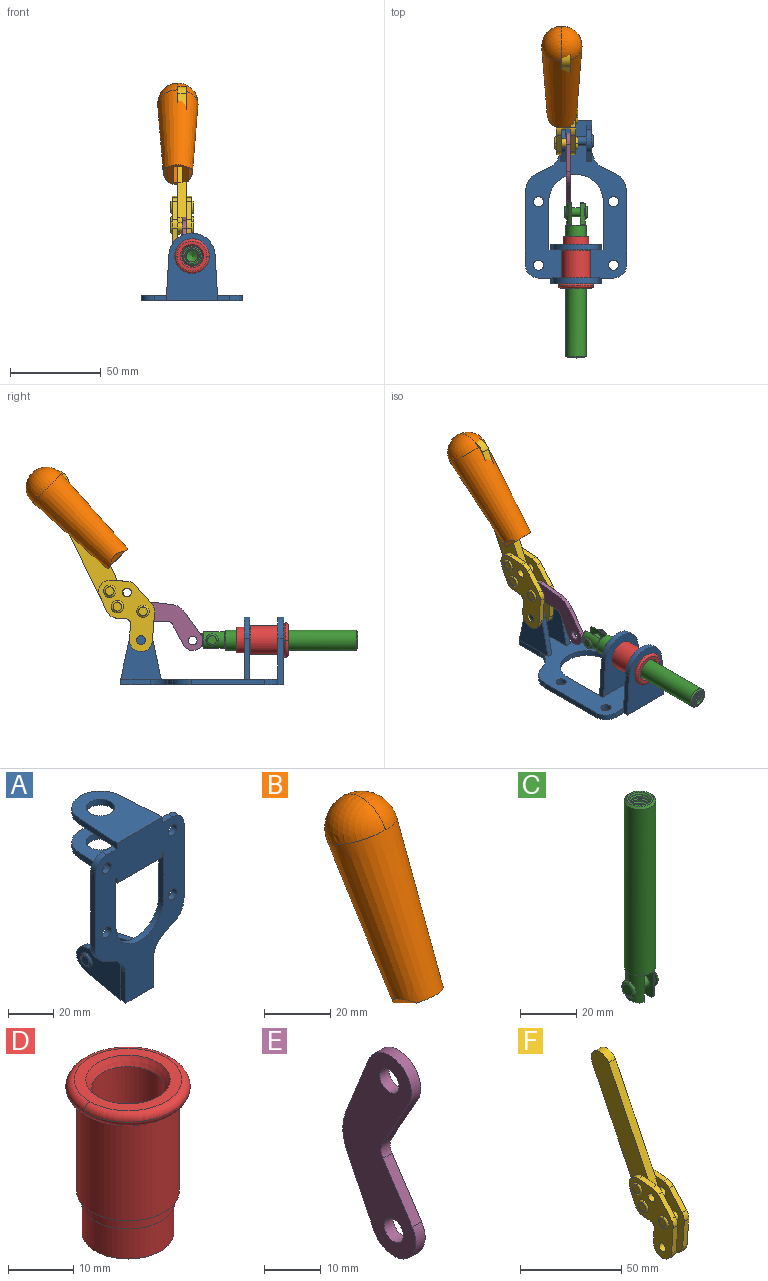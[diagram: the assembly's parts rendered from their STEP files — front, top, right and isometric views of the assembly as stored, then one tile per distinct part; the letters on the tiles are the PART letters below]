
ASSEMBLY  parts=6 mates=5
PART A: 55 faces, bbox 55.7x37.4x89.8 mm
  f0: torus R=2.41mm, axis (-1,0,0), area 15mm2, adj f11,f15,f25
  f1: torus R=2.41mm, axis (-1,0,0), area 15mm2, adj f10,f12,f22
  f2: cylinder r=2.78mm len=5.56mm, axis (0,-1,0), area 54.2mm2, adj f30,f54
  f3: cylinder r=14.99mm len=29.97mm, axis (0,-1,0), area 145.9mm2, adj f30,f49,f53,f54
  f4: cylinder r=2.78mm len=5.56mm, axis (0,-1,0), area 54.2mm2, adj f30,f54
  f5: cylinder r=2.78mm len=5.56mm, axis (0,-1,0), area 54.2mm2, adj f30,f54
  f6: cylinder r=2.78mm len=5.56mm, axis (0,-1,0), area 54.2mm2, adj f30,f54
  f7: cylinder r=6.35mm len=12.7mm, axis (0,0,1), area 123.6mm2, adj f27,f51
  f8: cylinder r=6.35mm len=12.7mm, axis (0,0,-1), area 124.7mm2, adj f21,f35
  f9: cylinder r=2.41mm len=11.18mm, axis (-1,0,0), area 169.4mm2, adj f16,f19
  f10: plane 4.83x4.83mm, normal (1,0,0), area 18.3mm2, adj f1,f12
  f11: plane 4.83x4.83mm, normal (-1,0,0), area 18.3mm2, adj f0,f15
  f12: torus R=2.41mm, axis (-1,0,0), area 15mm2, adj f1,f10,f22
  f13: cylinder r=6.35mm len=12.41mm, axis (1,0,0), area 53.4mm2, adj f18,f19,f22,f23
  f14: cylinder r=6.35mm len=12.41mm, axis (-1,0,0), area 53.4mm2, adj f16,f17,f24,f25
  f15: torus R=2.41mm, axis (-1,0,0), area 15mm2, adj f0,f11,f25
  f16: plane 27.86x22.35mm, normal (1,0,0), area 425.4mm2, adj f9,f14,f17,f24,f30
  f17: plane 22.86x4.97mm, normal (0,0.21,0.98), area 72.5mm2, adj f14,f16,f25,f30
  f18: plane 22.86x4.97mm, normal (0,0.21,0.98), area 72.5mm2, adj f13,f19,f22,f30
  f19: plane 27.86x22.35mm, normal (-1,0,0), area 425.4mm2, adj f9,f13,f18,f23,f30
  f20: cylinder r=12.7mm len=25.35mm, axis (0,0,-1), area 119.8mm2, adj f21,f34,f35,f36
  f21: plane 34.21x28.07mm, normal (0,0,-1), area 702.4mm2, adj f8,f20,f30,f34,f36
  f22: plane 27.96x22.45mm, normal (1,0,0), area 407.2mm2, adj f1,f12,f13,f18,f23,f30,f42,f43
  f23: plane 22.86x4.97mm, normal (0,0.21,-0.98), area 72.5mm2, adj f13,f19,f22,f44
  f24: plane 22.86x4.97mm, normal (0,0.21,-0.98), area 72.5mm2, adj f14,f16,f25,f44
  f25: plane 27.86x22.35mm, normal (-1,0,0), area 407.1mm2, adj f0,f14,f15,f17,f24,f30,f45,f46
  f26: plane 3.1x0.95mm, normal (0,0,-1), area 2.7mm2, adj f30,f49,f50,f54
  f27: plane 34.21x28.07mm, normal (0,0,1), area 702.4mm2, adj f7,f28,f30,f50,f52
  f28: cylinder r=12.7mm len=25.35mm, axis (0,0,1), area 118.8mm2, adj f27,f50,f51,f52
  f29: plane 3.1x0.95mm, normal (0,0,-1), area 2.7mm2, adj f30,f52,f53,f54
  f30: plane 86.54x55.63mm, normal (0,1,0), area 2362.9mm2, adj f2,f3,f4,f5,f6,f16,f17,f18
  f31: plane 40.56x3.1mm, normal (-1,0,0), area 125.7mm2, adj f30,f32,f48,f54
  f32: cylinder r=7.11mm len=7.11mm, axis (0,-1,0), area 34.6mm2, adj f30,f31,f33,f54
  f33: plane 6.67x3.1mm, normal (0,0,1), area 20.4mm2, adj f30,f32,f34,f54
  f34: plane 25.39x3.13mm, normal (-1,0.06,0), area 79.5mm2, adj f20,f21,f33,f35,f54
  f35: plane 37.31x28.45mm, normal (0,0,1), area 789.9mm2, adj f8,f20,f34,f36,f54
  f36: plane 25.39x3.13mm, normal (1,0.06,0), area 79.5mm2, adj f20,f21,f35,f37,f54
  f37: plane 6.67x3.1mm, normal (0,0,1), area 20.4mm2, adj f30,f36,f38,f54
  f38: cylinder r=7.11mm len=7.11mm, axis (0,-1,0), area 34.6mm2, adj f30,f37,f39,f54
  f39: plane 40.56x3.1mm, normal (1,0,0), area 125.7mm2, adj f30,f38,f40,f54
  f40: cylinder r=11.18mm len=10.16mm, axis (0,-1,0), area 39.5mm2, adj f30,f39,f41,f54
  f41: plane 6.09x3.1mm, normal (0.42,0,-0.91), area 20.8mm2, adj f30,f40,f42,f54
  f42: cylinder r=11.18mm len=9.41mm, axis (0,-1,0), area 37.2mm2, adj f22,f30,f41,f43,f54
  f43: plane 16.5x3.1mm, normal (1,0,0), area 51.1mm2, adj f22,f42,f44,f54
  f44: plane 17.37x3.1mm, normal (0,0,-1), area 53.8mm2, adj f23,f24,f30,f43,f45,f54
  f45: plane 16.5x3.1mm, normal (-1,0,0), area 51.1mm2, adj f25,f44,f46,f54
  f46: cylinder r=11.18mm len=9.41mm, axis (0,-1,0), area 37.2mm2, adj f25,f30,f45,f47,f54
  f47: plane 6.09x3.1mm, normal (-0.42,0,-0.91), area 20.8mm2, adj f30,f46,f48,f54
  f48: cylinder r=11.18mm len=10.16mm, axis (0,-1,0), area 39.5mm2, adj f30,f31,f47,f54
  f49: plane 26.54x3.1mm, normal (-1,0,0), area 82.3mm2, adj f3,f26,f30,f54
  f50: plane 25.39x3.1mm, normal (1,0.06,0), area 78.8mm2, adj f26,f27,f28,f51,f54
  f51: plane 37.31x28.45mm, normal (0,0,-1), area 789.9mm2, adj f7,f28,f50,f52,f54
  f52: plane 25.39x3.1mm, normal (-1,0.06,0), area 78.8mm2, adj f27,f28,f29,f51,f54
  f53: plane 26.54x3.1mm, normal (1,0,0), area 82.3mm2, adj f3,f29,f30,f54
  f54: plane 89.66x55.63mm, normal (0,-1,0), area 2678.5mm2, adj f2,f3,f4,f5,f6,f26,f29,f31
PART B: 11 faces, bbox 22.3x42.6x64.5 mm
  f0: sphere r=11.13mm, area 411.4mm2, adj f1,f8
  f1: cone r=11.11mm half-angle=3.3deg, axis (0,0.44,0.9), area 3251.8mm2, adj f0,f7,f8,f9,f10
  f2: cylinder r=6.16mm len=11.7mm, axis (1,0,0), area 89.5mm2, adj f3,f4,f5,f6
  f3: plane 60.23x36.75mm, normal (-1,0,0), area 763.6mm2, adj f2,f4,f6,f10
  f4: plane 51.37x25.05mm, normal (0,0.9,-0.44), area 264.2mm2, adj f2,f3,f5,f10
  f5: plane 60.23x36.75mm, normal (1,0,0), area 763.6mm2, adj f2,f4,f6,f10
  f6: plane 51.37x25.05mm, normal (0,-0.9,0.44), area 264.2mm2, adj f2,f3,f5,f10
  f7: plane 9.95x5.95mm, normal (0.71,-0.31,-0.64), area 25.8mm2, adj f1,f10
  f8: sphere r=11.13mm, area 411.4mm2, adj f0,f1
  f9: plane 9.95x5.95mm, normal (-0.71,-0.31,-0.64), area 25.8mm2, adj f1,f10
  f10: plane 14.27x11.38mm, normal (0,-0.44,-0.9), area 106.7mm2, adj f1,f3,f4,f5,f6,f7,f9
PART C: 48 faces, bbox 12.6x11.1x86.1 mm
  f0: torus R=2.41mm, axis (-1,0,0), area 15mm2, adj f30,f32,f34
  f1: torus R=2.41mm, axis (-1,0,0), area 15mm2, adj f29,f31,f33
  f2: cylinder r=5.54mm len=72.39mm, axis (0,0,1), area 2518.5mm2, adj f3,f4,f42,f43
  f3: cone r=5.54mm half-angle=45deg, axis (0,0,1), area 7.6mm2, adj f2,f5,f41
  f4: cone r=5.54mm half-angle=45deg, axis (0,0,-1), area 34.9mm2, adj f2,f39
  f5: cylinder r=5.08mm len=11.48mm, axis (0,0,1), area 108.3mm2, adj f3,f7,f8,f41
  f6: cylinder r=2.41mm len=4.83mm, axis (-1,0,0), area 71.2mm2, adj f40,f41
  f7: cylinder r=2.41mm len=4.83mm, axis (-1,0,0), area 7.6mm2, adj f5,f34
  f8: cone r=5.08mm half-angle=45deg, axis (0,0,1), area 10.6mm2, adj f5,f37,f41
  f9: cone r=3.98mm half-angle=45deg, axis (0,0,1), area 17.6mm2, adj f27,f39,f45,f46,f47
  f10: cylinder r=2.41mm len=4.83mm, axis (-1,0,0), area 7.6mm2, adj f33,f38
  f11: cylinder r=3.2mm len=6.4mm, axis (0,0,1), area 78.4mm2, adj f12,f28,f44,f45,f47
  f12: cylinder r=3.2mm len=6.4mm, axis (0,0,1), area 10.5mm2, adj f11,f13,f45,f47
  f13: cylinder r=3.2mm len=6.4mm, axis (0,0,1), area 10.5mm2, adj f12,f14,f45,f47
  f14: cylinder r=3.2mm len=6.4mm, axis (0,0,1), area 10.5mm2, adj f13,f15,f45,f47
  f15: cylinder r=3.2mm len=6.4mm, axis (0,0,1), area 10.5mm2, adj f14,f16,f45,f47
  f16: cylinder r=3.2mm len=6.4mm, axis (0,0,1), area 10.5mm2, adj f15,f17,f45,f47
  f17: cylinder r=3.2mm len=6.4mm, axis (0,0,1), area 10.5mm2, adj f16,f18,f45,f47
  f18: cylinder r=3.2mm len=6.4mm, axis (0,0,1), area 10.5mm2, adj f17,f19,f45,f47
  f19: cylinder r=3.2mm len=6.4mm, axis (0,0,1), area 10.5mm2, adj f18,f20,f45,f47
  f20: cylinder r=3.2mm len=6.4mm, axis (0,0,1), area 10.5mm2, adj f19,f21,f45,f47
  f21: cylinder r=3.2mm len=6.4mm, axis (0,0,1), area 10.5mm2, adj f20,f22,f45,f47
  f22: cylinder r=3.2mm len=6.4mm, axis (0,0,1), area 10.5mm2, adj f21,f23,f45,f47
  f23: cylinder r=3.2mm len=6.4mm, axis (0,0,1), area 10.5mm2, adj f22,f24,f45,f47
  f24: cylinder r=3.2mm len=6.4mm, axis (0,0,1), area 10.5mm2, adj f23,f25,f45,f47
  f25: cylinder r=3.2mm len=6.4mm, axis (0,0,1), area 10.5mm2, adj f24,f26,f45,f47
  f26: cylinder r=3.2mm len=6.4mm, axis (0,0,1), area 10.5mm2, adj f25,f27,f45,f47
  f27: cylinder r=3.2mm len=6.4mm, axis (0,0,1), area 7.4mm2, adj f9,f26,f45,f47
  f28: cone r=3.2mm half-angle=60deg, axis (0,0,1), area 37.2mm2, adj f11
  f29: plane 4.83x4.83mm, normal (-1,0,0), area 18.3mm2, adj f1,f31
  f30: plane 4.83x4.83mm, normal (1,0,0), area 18.3mm2, adj f0,f32
  f31: torus R=2.41mm, axis (-1,0,0), area 15mm2, adj f1,f29,f33
  f32: torus R=2.41mm, axis (-1,0,0), area 15mm2, adj f0,f30,f34
  f33: plane 6.83x6.83mm, normal (1,0,0), area 18.3mm2, adj f1,f10,f31
  f34: plane 6.83x6.83mm, normal (-1,0,0), area 18.3mm2, adj f0,f7,f32
  f35: cone r=5.08mm half-angle=45deg, axis (0,0,1), area 10.6mm2, adj f36,f38,f40
  f36: plane 7.25x1.97mm, normal (0,0,-1), area 10mm2, adj f35,f40
  f37: plane 7.25x1.97mm, normal (0,0,-1), area 10mm2, adj f8,f41
  f38: cylinder r=5.08mm len=11.48mm, axis (0,0,1), area 108.3mm2, adj f10,f35,f40,f42
  f39: plane 9.55x9.55mm, normal (0,0,1), area 22mm2, adj f4,f9
  f40: plane 12.76x10.09mm, normal (1,0,0), area 95.7mm2, adj f6,f35,f36,f38,f42,f43
  f41: plane 12.76x10.09mm, normal (-1,0,0), area 95.7mm2, adj f3,f5,f6,f8,f37,f43
  f42: cone r=5.54mm half-angle=45deg, axis (0,0,1), area 7.6mm2, adj f2,f38,f40
  f43: plane 11.07x4.7mm, normal (0,0,-1), area 50.4mm2, adj f2,f40,f41
  f44: plane 0.89x0.62mm, normal (-1,0,0), area 0.3mm2, adj f11,f45,f46,f47
  f45: bspline ~24.8x7.63mm, area 266.6mm2, adj f9,f11,f12,f13,f14,f15,f16,f17
  f46: bspline ~24.87x7.63mm, area 73.6mm2, adj f9,f44,f45,f47
  f47: bspline ~24.98x7.63mm, area 272.5mm2, adj f9,f11,f12,f13,f14,f15,f16,f17
PART D: 15 faces, bbox 20.6x20.6x28.7 mm
  f0: torus R=8.26mm, axis (0,0,1), area 56.8mm2, adj f1,f10,f12
  f1: torus R=8.26mm, axis (0,0,1), area 56.8mm2, adj f0,f6,f13
  f2: cylinder r=5.59mm len=25.91mm, axis (0,0,1), area 909.6mm2, adj f3,f4
  f3: cone r=6.86mm half-angle=45deg, axis (0,0,-1), area 70.2mm2, adj f2,f14
  f4: cone r=6.47mm half-angle=30deg, axis (0,0,1), area 66.7mm2, adj f2,f13
  f5: cylinder r=7.04mm len=14.07mm, axis (0,0,1), area 252.6mm2, adj f11,f14
  f6: torus R=8.26mm, axis (0,0,1), area 56.8mm2, adj f1,f12,f13
  f7: cylinder r=7.16mm len=14.33mm, axis (0,0,1), area 91.5mm2, adj f9,f11
  f8: cylinder r=7.86mm len=18.42mm, axis (0,0,1), area 909.6mm2, adj f9,f10
  f9: plane 15.72x15.72mm, normal (0,0,-1), area 33mm2, adj f7,f8
  f10: plane 16.51x16.51mm, normal (0,0,-1), area 19.9mm2, adj f0,f8,f12
  f11: plane 14.33x14.33mm, normal (0,0,-1), area 5.7mm2, adj f5,f7
  f12: torus R=8.26mm, axis (0,0,1), area 56.8mm2, adj f0,f6,f10
  f13: plane 16.51x16.51mm, normal (0,0,1), area 82.7mm2, adj f1,f4,f6
  f14: plane 14.07x14.07mm, normal (0,0,-1), area 7.8mm2, adj f3,f5
PART E: 12 faces, bbox 2.3x18.2x42.8 mm
  f0: cylinder r=2.4mm len=4.8mm, axis (1,0,0), area 34.9mm2, adj f4,f11
  f1: cylinder r=10.41mm len=8.47mm, axis (1,0,0), area 20.2mm2, adj f4,f9,f10,f11
  f2: cylinder r=3.05mm len=3.16mm, axis (1,0,0), area 7.7mm2, adj f4,f6,f7,f11
  f3: cylinder r=2.4mm len=4.8mm, axis (1,0,0), area 34.9mm2, adj f4,f11
  f4: plane 42.81x18.23mm, normal (-1,0,0), area 414.1mm2, adj f0,f1,f2,f3,f5,f6,f7,f8
  f5: cylinder r=5.54mm len=10.67mm, axis (1,0,0), area 41.8mm2, adj f4,f6,f10,f11
  f6: plane 11.66x6.53mm, normal (0,-0.87,-0.49), area 30.9mm2, adj f2,f4,f5,f11
  f7: plane 11.17x7.33mm, normal (0,-0.84,0.55), area 30.9mm2, adj f2,f4,f8,f11
  f8: cylinder r=5.54mm len=10.51mm, axis (1,0,0), area 41.8mm2, adj f4,f7,f9,f11
  f9: plane 13.67x6.67mm, normal (0,0.9,-0.44), area 35.1mm2, adj f1,f4,f8,f11
  f10: plane 14.1x5.7mm, normal (0,0.93,0.37), area 35.1mm2, adj f1,f4,f5,f11
  f11: plane 42.81x18.23mm, normal (1,0,0), area 414.1mm2, adj f0,f1,f2,f3,f5,f6,f7,f8
PART F: 59 faces, bbox 12.9x60.2x99.6 mm
  f0: torus R=2.39mm, axis (-1,0,0), area 14.9mm2, adj f20,f43,f51
  f1: torus R=2.39mm, axis (-1,0,0), area 14.9mm2, adj f19,f42,f51
  f2: torus R=2.39mm, axis (-1,0,0), area 14.9mm2, adj f18,f35,f51
  f3: torus R=2.39mm, axis (-1,0,0), area 14.9mm2, adj f14,f17,f23
  f4: torus R=2.39mm, axis (-1,0,0), area 14.9mm2, adj f13,f16,f23
  f5: torus R=2.39mm, axis (-1,0,0), area 14.9mm2, adj f12,f15,f23
  f6: cylinder r=2.39mm len=4.78mm, axis (1,0,0), area 46.5mm2, adj f48,f50,f51
  f7: cylinder r=2.39mm len=4.78mm, axis (1,0,0), area 46.5mm2, adj f50,f51
  f8: cylinder r=6.35mm len=12.68mm, axis (1,0,0), area 61.8mm2, adj f38,f39,f50,f51
  f9: cylinder r=2.39mm len=4.78mm, axis (-1,0,0), area 70.5mm2, adj f46,f50
  f10: cylinder r=2.39mm len=4.78mm, axis (-1,0,0), area 46.5mm2, adj f23,f45,f46
  f11: cylinder r=2.39mm len=4.78mm, axis (-1,0,0), area 46.5mm2, adj f23,f46
  f12: plane 4.78x4.78mm, normal (1,0,0), area 17.9mm2, adj f5,f15
  f13: plane 4.78x4.78mm, normal (1,0,0), area 17.9mm2, adj f4,f16
  f14: plane 4.78x4.78mm, normal (1,0,0), area 17.9mm2, adj f3,f17
  f15: torus R=2.39mm, axis (-1,0,0), area 14.9mm2, adj f5,f12,f23
  f16: torus R=2.39mm, axis (-1,0,0), area 14.9mm2, adj f4,f13,f23
  f17: torus R=2.39mm, axis (-1,0,0), area 14.9mm2, adj f3,f14,f23
  f18: plane 4.78x4.78mm, normal (-1,0,0), area 17.9mm2, adj f2,f35
  f19: plane 4.78x4.78mm, normal (-1,0,0), area 17.9mm2, adj f1,f42
  f20: plane 4.78x4.78mm, normal (-1,0,0), area 17.9mm2, adj f0,f43
  f21: plane 2.26x0.2mm, normal (1,0,0), area 0.2mm2, adj f31,f44
  f22: plane 2.26x0.2mm, normal (-1,0,0), area 0.2mm2, adj f41,f44
  f23: plane 39.37x30.77mm, normal (1,0,0), area 565.5mm2, adj f3,f4,f5,f10,f11,f15,f16,f17
  f24: cylinder r=6.1mm len=4.15mm, axis (-1,0,0), area 14.7mm2, adj f23,f25,f32,f46
  f25: plane 10.25x9.01mm, normal (0,-0.75,0.66), area 42.3mm2, adj f23,f24,f26,f46
  f26: cylinder r=6.35mm len=4.64mm, axis (-1,0,0), area 15.6mm2, adj f23,f25,f27,f46
  f27: plane 15.84x3.1mm, normal (0,-1,-0.07), area 49.2mm2, adj f23,f26,f28,f46
  f28: cylinder r=6.35mm len=12.68mm, axis (-1,0,0), area 61.8mm2, adj f23,f27,f29,f46
  f29: plane 8.11x3.1mm, normal (0,1,0.07), area 25.2mm2, adj f23,f28,f30,f46
  f30: cylinder r=3.05mm len=3.25mm, axis (-1,0,0), area 14.8mm2, adj f23,f29,f31,f46
  f31: plane 5.99x3.1mm, normal (0,0.07,-1), area 18.6mm2, adj f21,f23,f30,f44,f46
  f32: plane 9.5x3.1mm, normal (0,-0.07,1), area 29.5mm2, adj f23,f24,f33,f46,f47
  f33: cylinder r=6.1mm len=8.63mm, axis (-1,0,0), area 39.1mm2, adj f23,f32,f34,f47
  f34: plane 8.65x3.96mm, normal (0,0.91,-0.42), area 29.5mm2, adj f23,f33,f44,f47
  f35: torus R=2.39mm, axis (-1,0,0), area 14.9mm2, adj f2,f18,f51
  f36: plane 10.25x9.01mm, normal (0,-0.75,0.66), area 42.3mm2, adj f37,f49,f50,f51
  f37: cylinder r=6.35mm len=4.64mm, axis (1,0,0), area 15.6mm2, adj f36,f38,f50,f51
  f38: plane 15.84x3.1mm, normal (0,-1,-0.07), area 49.2mm2, adj f8,f37,f50,f51
  f39: plane 8.11x3.1mm, normal (0,1,0.07), area 25.2mm2, adj f8,f40,f50,f51
  f40: cylinder r=3.05mm len=3.25mm, axis (1,0,0), area 14.8mm2, adj f39,f41,f50,f51
  f41: plane 5.99x3.1mm, normal (0,0.07,-1), area 18.6mm2, adj f22,f40,f44,f50,f51
  f42: torus R=2.39mm, axis (-1,0,0), area 14.9mm2, adj f1,f19,f51
  f43: torus R=2.39mm, axis (-1,0,0), area 14.9mm2, adj f0,f20,f51
  f44: cylinder r=6.35mm len=12.12mm, axis (-1,0,0), area 128.9mm2, adj f21,f22,f23,f31,f34,f41,f46,f47
  f45: plane 2.65x1.35mm, normal (1,0,0), area 1mm2, adj f10,f55
  f46: plane 39.08x20.42mm, normal (-1,0,0), area 412.5mm2, adj f9,f10,f11,f24,f25,f26,f27,f28
  f47: plane 77.62x39.82mm, normal (1,0,0), area 850mm2, adj f32,f33,f34,f44,f53,f54,f55
  f48: plane 2.65x1.35mm, normal (-1,0,0), area 1mm2, adj f6,f55
  f49: cylinder r=6.1mm len=4.15mm, axis (1,0,0), area 14.7mm2, adj f36,f50,f51,f56
  f50: plane 39.08x20.42mm, normal (1,0,0), area 412.5mm2, adj f6,f7,f8,f9,f36,f37,f38,f39
  f51: plane 39.37x30.77mm, normal (-1,0,0), area 565.5mm2, adj f0,f1,f2,f6,f7,f8,f35,f36
  f52: plane 8.65x3.96mm, normal (0,0.91,-0.42), area 29.5mm2, adj f44,f51,f57,f58
  f53: plane 68.49x33.4mm, normal (0,0.9,-0.44), area 358.1mm2, adj f44,f47,f54,f58
  f54: cylinder r=6.35mm len=12.06mm, axis (1,0,0), area 93.7mm2, adj f47,f53,f55,f58
  f55: plane 68.49x33.4mm, normal (0,-0.9,0.44), area 358.1mm2, adj f44,f45,f46,f47,f48,f50,f54,f58
  f56: plane 9.5x3.1mm, normal (0,-0.07,1), area 29.5mm2, adj f49,f50,f51,f57,f58
  f57: cylinder r=6.1mm len=8.63mm, axis (1,0,0), area 39.1mm2, adj f51,f52,f56,f58
  f58: plane 77.62x39.82mm, normal (-1,0,0), area 850mm2, adj f44,f52,f53,f54,f55,f56,f57
PLACE A rot(axis=(1,0,0),90deg) t=(0,9.43,0)mm fixed
PLACE B rot(axis=(-1,0,0),19deg) t=(-7.8,9.79,81.17)mm
PLACE C rot(axis=(1,0,0),90deg) t=(0,17.84,0)mm
PLACE D rot(axis=(1,0,0),90deg) t=(0,9.43,0)mm
PLACE E rot(axis=(0,-0.51,-0.86),180deg) t=(-4.29,38.57,11.43)mm
PLACE F rot(axis=(1,0,0),0deg) t=(-5.45,16.91,56.71)mm
MATE fastened D.f2 <-> A.f7  axis (0,-1,0) through (0,-36.96,24.61)mm
MATE slider D.f2 <-> C.f2  axis (0,-1,0) through (0,-39.5,24.61)mm
MATE fastened A.f0 <-> F.f7  axis (-1,0,0) through (0,41.52,24.61)mm
MATE fastened F.f58 <-> B.f0  axis (-1,0,0) through (-7.8,93.66,108.7)mm
MATE revolute F.f4 <-> E.f5  axis (-1,0,0) through (-5.45,40.42,40.45)mm
